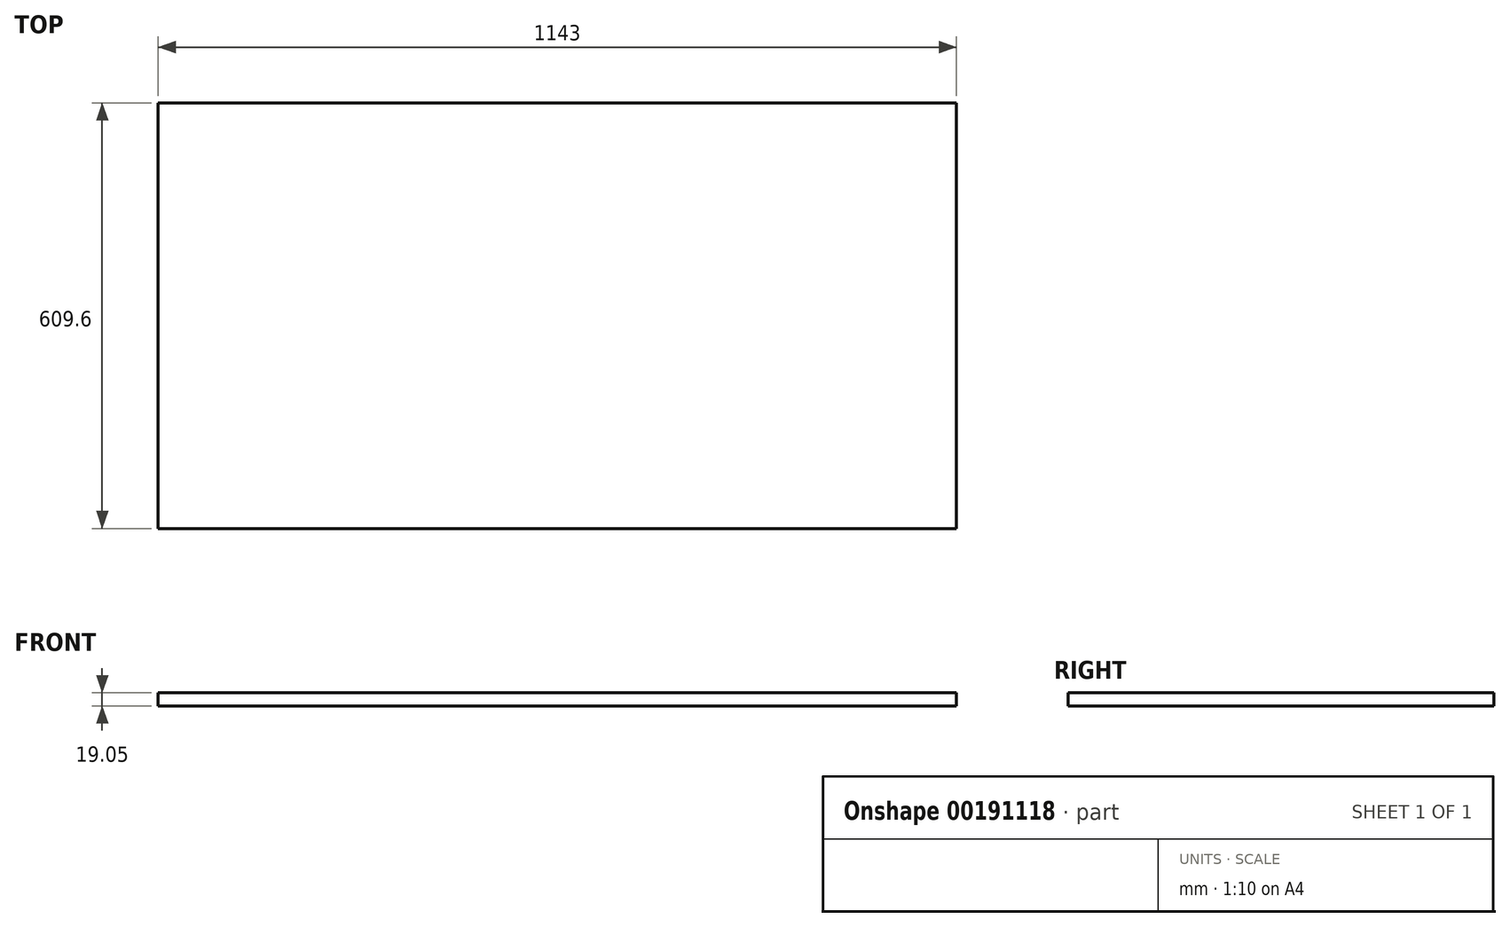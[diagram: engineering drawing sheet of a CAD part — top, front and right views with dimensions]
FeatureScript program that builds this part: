
annotation { "Feature Type Name" : "Feature", "Feature Type Description" : "" }
export const myFeature = defineFeature(function(context is Context, id is Id, definition is map)
    precondition{}
    {
        {
            var Q0;
            Q0=qCreatedBy(makeId("Top.planeOp"),FACE);
            var sketch = newSketch(context, id + "F0", { "sketchPlane" : qUnion([Q0])});
            skLineSegment(sketch, "E0.bottom", {"start": v(571.5, 304.8) * mm, "end": v(-571.5, 304.8) * mm});
            skLineSegment(sketch, "E0.top", {"start": v(571.5, -304.8) * mm, "end": v(-571.5, -304.8) * mm});
            skLineSegment(sketch, "E0.left", {"start": v(571.5, 304.8) * mm, "end": v(571.5, -304.8) * mm});
            skLineSegment(sketch, "E0.right", {"start": v(-571.5, 304.8) * mm, "end": v(-571.5, -304.8) * mm});
            skPoint(sketch, "E0.middle", {"position": v(0, 0) * mm});
            skSolve(sketch);
        }
        {
            var Q0;
            Q0 = qSketchRegion(id + "F0", true);
            extrude(context, id + "F1", {"entities" : qUnion([Q0]), "depth" : 19.05 * mm});
        }
    });
